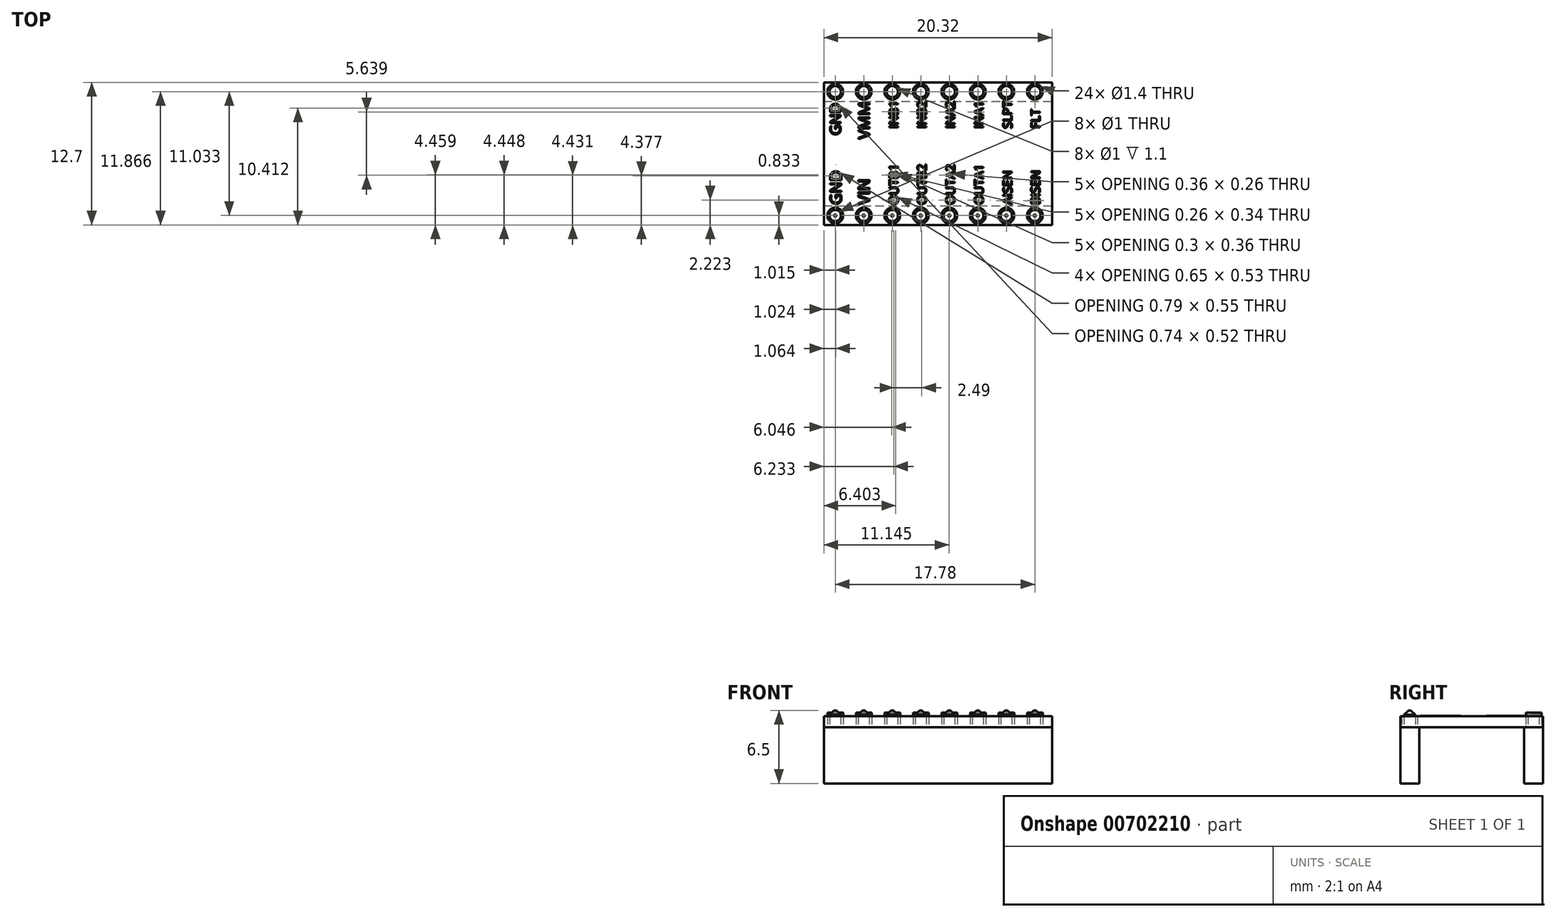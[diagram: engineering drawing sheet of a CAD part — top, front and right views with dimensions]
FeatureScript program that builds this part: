
annotation { "Feature Type Name" : "Feature", "Feature Type Description" : "" }
export const myFeature = defineFeature(function(context is Context, id is Id, definition is map)
    precondition{}
    {
        {
            var Q0;
            Q0=qCreatedBy(makeId("Top.planeOp"),FACE);
            cPlane(context, id + "F0", {"entities" : qUnion([Q0]), "cplaneType" : CPlaneType.OFFSET, "offset" : 5 * mm, "width" : 150 * mm, "height" : 150 * mm});
        }
        {
            var Q0;
            Q0=qCreatedBy(id+"F0.planeOp",FACE);
            var sketch = newSketch(context, id + "F1", { "sketchPlane" : qUnion([Q0])});
            skLineSegment(sketch, "E0.bottom", {"start": v(-10.16, 6.35) * mm, "end": v(10.16, 6.35) * mm});
            skLineSegment(sketch, "E0.top", {"start": v(-10.16, -6.35) * mm, "end": v(10.16, -6.35) * mm});
            skLineSegment(sketch, "E0.left", {"start": v(-10.16, 6.35) * mm, "end": v(-10.16, -6.35) * mm});
            skLineSegment(sketch, "E0.right", {"start": v(10.16, 6.35) * mm, "end": v(10.16, -6.35) * mm});
            skPoint(sketch, "E0.middle", {"position": v(0, 0) * mm});
            skCircle(sketch, "E1", {"center": v(-9.15, -5.52) * mm, "radius": 0.5 * mm});
            skCircle(sketch, "E2.0", {"center": v(-9.15, -5.52) * mm, "radius": 0.7 * mm});
            skCircle(sketch, "E3.1.0.0", {"center": v(-6.6, -5.52) * mm, "radius": 0.5 * mm});
            skCircle(sketch, "E3.1.0.1", {"center": v(-6.6, -5.52) * mm, "radius": 0.7 * mm});
            skCircle(sketch, "E3.2.0.0", {"center": v(-4.07, -5.52) * mm, "radius": 0.5 * mm});
            skCircle(sketch, "E3.2.0.1", {"center": v(-4.07, -5.52) * mm, "radius": 0.7 * mm});
            skCircle(sketch, "E3.3.0.0", {"center": v(-1.53, -5.52) * mm, "radius": 0.5 * mm});
            skCircle(sketch, "E3.3.0.1", {"center": v(-1.53, -5.52) * mm, "radius": 0.7 * mm});
            skCircle(sketch, "E3.4.0.0", {"center": v(1.01, -5.52) * mm, "radius": 0.5 * mm});
            skCircle(sketch, "E3.4.0.1", {"center": v(1.01, -5.52) * mm, "radius": 0.7 * mm});
            skCircle(sketch, "E3.5.0.0", {"center": v(3.55, -5.52) * mm, "radius": 0.5 * mm});
            skCircle(sketch, "E3.5.0.1", {"center": v(3.55, -5.52) * mm, "radius": 0.7 * mm});
            skCircle(sketch, "E3.6.0.0", {"center": v(6.1, -5.52) * mm, "radius": 0.5 * mm});
            skCircle(sketch, "E3.6.0.1", {"center": v(6.1, -5.52) * mm, "radius": 0.7 * mm});
            skCircle(sketch, "E3.7.0.0", {"center": v(8.63, -5.52) * mm, "radius": 0.5 * mm});
            skCircle(sketch, "E3.7.0.1", {"center": v(8.63, -5.52) * mm, "radius": 0.7 * mm});
            skLineSegment(sketch, "E3.direction1", {"start": v(-9.15, -5.52) * mm, "end": v(-6.6, -5.52) * mm, "construction": true});
            skCircle(sketch, "E4.MirrorC", {"center": v(-9.15, 5.52) * mm, "radius": 0.5 * mm});
            skCircle(sketch, "E5.MirrorC", {"center": v(-9.15, 5.52) * mm, "radius": 0.7 * mm});
            skCircle(sketch, "E6.MirrorC", {"center": v(-6.6, 5.52) * mm, "radius": 0.7 * mm});
            skCircle(sketch, "E7.MirrorC", {"center": v(-6.6, 5.52) * mm, "radius": 0.5 * mm});
            skCircle(sketch, "E8.MirrorC", {"center": v(-4.07, 5.52) * mm, "radius": 0.7 * mm});
            skCircle(sketch, "E9.MirrorC", {"center": v(-4.07, 5.52) * mm, "radius": 0.5 * mm});
            skCircle(sketch, "E10.MirrorC", {"center": v(-1.53, 5.52) * mm, "radius": 0.7 * mm});
            skCircle(sketch, "E11.MirrorC", {"center": v(-1.53, 5.52) * mm, "radius": 0.5 * mm});
            skCircle(sketch, "E12.MirrorC", {"center": v(1.01, 5.52) * mm, "radius": 0.7 * mm});
            skCircle(sketch, "E13.MirrorC", {"center": v(1.01, 5.52) * mm, "radius": 0.5 * mm});
            skCircle(sketch, "E14.MirrorC", {"center": v(3.55, 5.52) * mm, "radius": 0.5 * mm});
            skCircle(sketch, "E15.MirrorC", {"center": v(3.55, 5.52) * mm, "radius": 0.7 * mm});
            skCircle(sketch, "E16.MirrorC", {"center": v(6.1, 5.52) * mm, "radius": 0.7 * mm});
            skCircle(sketch, "E17.MirrorC", {"center": v(6.1, 5.52) * mm, "radius": 0.5 * mm});
            skCircle(sketch, "E18.MirrorC", {"center": v(8.63, 5.52) * mm, "radius": 0.7 * mm});
            skCircle(sketch, "E19.MirrorC", {"center": v(8.63, 5.52) * mm, "radius": 0.5 * mm});
            skSolve(sketch);
        }
        {
            var Q0;
            Q0=makeQuery(id+"F1.imprint","IMPRINT",FACE,{"disambiguationData":[TD([[makeQuery(id+"F1.imprint","IMPRINT",EDGE,{"derivedFrom":sQuery(id+"F1.wireOp",EDGE,"E0.bottom")}),-1.0]])]});
            extrude(context, id + "F2", {"entities" : qUnion([Q0]), "depth" : 1 * mm, "offsetDistance" : 25 * mm});
        }
        {
            var Q0;
            Q0=makeQuery(id+"F1.imprint","IMPRINT",FACE,{"disambiguationData":[TD([[makeQuery(id+"F1.imprint","IMPRINT",EDGE,{"derivedFrom":sQuery(id+"F1.wireOp",EDGE,"E4.MirrorC")}),1.0]])]});
            var Q1;
            Q1=makeQuery(id+"F1.imprint","IMPRINT",FACE,{"disambiguationData":[TD([[makeQuery(id+"F1.imprint","IMPRINT",EDGE,{"derivedFrom":sQuery(id+"F1.wireOp",EDGE,"E6.MirrorC")}),-1.0]])]});
            var Q2;
            Q2=makeQuery(id+"F1.imprint","IMPRINT",FACE,{"disambiguationData":[TD([[makeQuery(id+"F1.imprint","IMPRINT",EDGE,{"derivedFrom":sQuery(id+"F1.wireOp",EDGE,"E8.MirrorC")}),-1.0]])]});
            var Q3;
            Q3=makeQuery(id+"F1.imprint","IMPRINT",FACE,{"disambiguationData":[TD([[makeQuery(id+"F1.imprint","IMPRINT",EDGE,{"derivedFrom":sQuery(id+"F1.wireOp",EDGE,"E10.MirrorC")}),-1.0]])]});
            var Q4;
            Q4=makeQuery(id+"F1.imprint","IMPRINT",FACE,{"disambiguationData":[TD([[makeQuery(id+"F1.imprint","IMPRINT",EDGE,{"derivedFrom":sQuery(id+"F1.wireOp",EDGE,"E12.MirrorC")}),-1.0]])]});
            var Q5;
            Q5=makeQuery(id+"F1.imprint","IMPRINT",FACE,{"disambiguationData":[TD([[makeQuery(id+"F1.imprint","IMPRINT",EDGE,{"derivedFrom":sQuery(id+"F1.wireOp",EDGE,"E14.MirrorC")}),1.0]])]});
            var Q6;
            Q6=makeQuery(id+"F1.imprint","IMPRINT",FACE,{"disambiguationData":[TD([[makeQuery(id+"F1.imprint","IMPRINT",EDGE,{"derivedFrom":sQuery(id+"F1.wireOp",EDGE,"E16.MirrorC")}),-1.0]])]});
            var Q7;
            Q7=makeQuery(id+"F1.imprint","IMPRINT",FACE,{"disambiguationData":[TD([[makeQuery(id+"F1.imprint","IMPRINT",EDGE,{"derivedFrom":sQuery(id+"F1.wireOp",EDGE,"E18.MirrorC")}),-1.0]])]});
            var Q8;
            Q8=makeQuery(id+"F1.imprint","IMPRINT",FACE,{"disambiguationData":[TD([[makeQuery(id+"F1.imprint","IMPRINT",EDGE,{"derivedFrom":sQuery(id+"F1.wireOp",EDGE,"E3.7.0.0")}),-1.0]])]});
            var Q9;
            Q9=makeQuery(id+"F1.imprint","IMPRINT",FACE,{"disambiguationData":[TD([[makeQuery(id+"F1.imprint","IMPRINT",EDGE,{"derivedFrom":sQuery(id+"F1.wireOp",EDGE,"E3.6.0.0")}),-1.0]])]});
            var Q10;
            Q10=makeQuery(id+"F1.imprint","IMPRINT",FACE,{"disambiguationData":[TD([[makeQuery(id+"F1.imprint","IMPRINT",EDGE,{"derivedFrom":sQuery(id+"F1.wireOp",EDGE,"E3.5.0.0")}),-1.0]])]});
            var Q11;
            Q11=makeQuery(id+"F1.imprint","IMPRINT",FACE,{"disambiguationData":[TD([[makeQuery(id+"F1.imprint","IMPRINT",EDGE,{"derivedFrom":sQuery(id+"F1.wireOp",EDGE,"E3.4.0.0")}),-1.0]])]});
            var Q12;
            Q12=makeQuery(id+"F1.imprint","IMPRINT",FACE,{"disambiguationData":[TD([[makeQuery(id+"F1.imprint","IMPRINT",EDGE,{"derivedFrom":sQuery(id+"F1.wireOp",EDGE,"E3.3.0.0")}),-1.0]])]});
            var Q13;
            Q13=makeQuery(id+"F1.imprint","IMPRINT",FACE,{"disambiguationData":[TD([[makeQuery(id+"F1.imprint","IMPRINT",EDGE,{"derivedFrom":sQuery(id+"F1.wireOp",EDGE,"E3.2.0.0")}),-1.0]])]});
            var Q14;
            Q14=makeQuery(id+"F1.imprint","IMPRINT",FACE,{"disambiguationData":[TD([[makeQuery(id+"F1.imprint","IMPRINT",EDGE,{"derivedFrom":sQuery(id+"F1.wireOp",EDGE,"E3.1.0.0")}),-1.0]])]});
            var Q15;
            Q15=makeQuery(id+"F1.imprint","IMPRINT",FACE,{"disambiguationData":[TD([[makeQuery(id+"F1.imprint","IMPRINT",EDGE,{"derivedFrom":sQuery(id+"F1.wireOp",EDGE,"E1")}),-1.0]])]});
            extrude(context, id + "F3", {"entities" : qUnion([Q0, Q1, Q2, Q3, Q4, Q5, Q6, Q7, Q8, Q9, Q10, Q11, Q12, Q13, Q14, Q15]), "depth" : 1 * mm, "offsetDistance" : 25 * mm});
        }
        {
            var Q0;
            Q0=qCreatedBy(id+"F0.planeOp",FACE);
            cPlane(context, id + "F4", {"entities" : qUnion([Q0]), "cplaneType" : CPlaneType.OFFSET, "offset" : 1 * mm, "width" : 150 * mm, "height" : 150 * mm});
        }
        {
            var Q0;
            Q0=qCreatedBy(id+"F4.planeOp",FACE);
            var sketch = newSketch(context, id + "F5", { "sketchPlane" : qUnion([Q0])});
            skText(sketch, "E20", { "text": "GND", "fontName": "OpenSans-Regular.ttf"});
            skText(sketch, "E21", { "text": "GND", "fontName": "OpenSans-Regular.ttf"});
            skText(sketch, "E22", { "text": "VIN", "fontName": "OpenSans-Regular.ttf"});
            skText(sketch, "E23", { "text": "VMM", "fontName": "OpenSans-Regular.ttf"});
            skText(sketch, "E24", { "text": "OUTB1", "fontName": "OpenSans-Regular.ttf"});
            skText(sketch, "E25", { "text": "OUTB2", "fontName": "OpenSans-Regular.ttf"});
            skText(sketch, "E26", { "text": "OUTA1", "fontName": "OpenSans-Regular.ttf"});
            skText(sketch, "E27", { "text": "OUTA2", "fontName": "OpenSans-Regular.ttf"});
            skText(sketch, "E28", { "text": "AISEN", "fontName": "OpenSans-Regular.ttf"});
            skText(sketch, "E29", { "text": "BISEN", "fontName": "OpenSans-Regular.ttf"});
            skText(sketch, "E30", { "text": "INA1", "fontName": "OpenSans-Regular.ttf"});
            skText(sketch, "E31", { "text": "INA2", "fontName": "OpenSans-Regular.ttf"});
            skText(sketch, "E32", { "text": "INB1", "fontName": "OpenSans-Regular.ttf"});
            skText(sketch, "E33", { "text": "INB2", "fontName": "OpenSans-Regular.ttf"});
            skText(sketch, "E34", { "text": "SLPT", "fontName": "OpenSans-Regular.ttf"});
            skText(sketch, "E35", { "text": "FLT", "fontName": "OpenSans-Regular.ttf"});
            const initialGuessF5  = {"E20": [-0.0086, -0.00456, 0, 1, 0.001], "E21": [-0.00867, 0.00163, 0, 1, 0.00094], "E22": [-0.00608, -0.00456, 0, 1, 0.00103], "E23": [-0.00608, 0.00129, 0, 1, 0.001], "E24": [-0.00353, -0.00456, 0, 1, 0.0008], "E25": [-0.00104, -0.00456, 0, 1, 0.0008], "E26": [0.00405, -0.00456, 0, 1, 0.0008], "E27": [0.0015, -0.00456, 0, 1, 0.0008], "E28": [0.0066, -0.00456, 0, 1, 0.0008], "E29": [0.00908, -0.00456, 0, 1, 0.0008], "E30": [0.00405, 0.00222, 0, 1, 0.0008], "E31": [0.0015, 0.00222, 0, 1, 0.0008], "E32": [-0.00353, 0.00222, 0, 1, 0.0008], "E33": [-0.00104, 0.00222, 0, 1, 0.0008], "E34": [0.0066, 0.00222, 0, 1, 0.0008], "E35": [0.00908, 0.00222, 0, 1, 0.0008]};
            skSetInitialGuess(sketch, initialGuessF5);
            skSolve(sketch);
        }
        {
            var Q0;
            Q0 = qSketchRegion(id + "F5", true);
            extrude(context, id + "F6", {"entities" : qUnion([Q0]), "depth" : 0.01 * mm, "offsetDistance" : 25 * mm});
        }
        {
            var Q0;
            Q0=makeQuery(id+"F1.imprint","IMPRINT",FACE,{"disambiguationData":[TD([[makeQuery(id+"F1.imprint","IMPRINT",EDGE,{"derivedFrom":sQuery(id+"F1.wireOp",EDGE,"E4.MirrorC")}),-1.0]])]});
            var Q1;
            Q1=makeQuery(id+"F1.imprint","IMPRINT",FACE,{"disambiguationData":[TD([[makeQuery(id+"F1.imprint","IMPRINT",EDGE,{"derivedFrom":sQuery(id+"F1.wireOp",EDGE,"E7.MirrorC")}),-1.0]])]});
            var Q2;
            Q2=makeQuery(id+"F1.imprint","IMPRINT",FACE,{"disambiguationData":[TD([[makeQuery(id+"F1.imprint","IMPRINT",EDGE,{"derivedFrom":sQuery(id+"F1.wireOp",EDGE,"E9.MirrorC")}),-1.0]])]});
            var Q3;
            Q3=makeQuery(id+"F1.imprint","IMPRINT",FACE,{"disambiguationData":[TD([[makeQuery(id+"F1.imprint","IMPRINT",EDGE,{"derivedFrom":sQuery(id+"F1.wireOp",EDGE,"E11.MirrorC")}),-1.0]])]});
            var Q4;
            Q4=makeQuery(id+"F1.imprint","IMPRINT",FACE,{"disambiguationData":[TD([[makeQuery(id+"F1.imprint","IMPRINT",EDGE,{"derivedFrom":sQuery(id+"F1.wireOp",EDGE,"E13.MirrorC")}),-1.0]])]});
            var Q5;
            Q5=makeQuery(id+"F1.imprint","IMPRINT",FACE,{"disambiguationData":[TD([[makeQuery(id+"F1.imprint","IMPRINT",EDGE,{"derivedFrom":sQuery(id+"F1.wireOp",EDGE,"E14.MirrorC")}),-1.0]])]});
            var Q6;
            Q6=makeQuery(id+"F1.imprint","IMPRINT",FACE,{"disambiguationData":[TD([[makeQuery(id+"F1.imprint","IMPRINT",EDGE,{"derivedFrom":sQuery(id+"F1.wireOp",EDGE,"E17.MirrorC")}),-1.0]])]});
            var Q7;
            Q7=makeQuery(id+"F1.imprint","IMPRINT",FACE,{"disambiguationData":[TD([[makeQuery(id+"F1.imprint","IMPRINT",EDGE,{"derivedFrom":sQuery(id+"F1.wireOp",EDGE,"E19.MirrorC")}),-1.0]])]});
            var Q8;
            Q8=makeQuery(id+"F1.imprint","IMPRINT",FACE,{"disambiguationData":[TD([[makeQuery(id+"F1.imprint","IMPRINT",EDGE,{"derivedFrom":sQuery(id+"F1.wireOp",EDGE,"E3.7.0.0")}),1.0]])]});
            var Q9;
            Q9=makeQuery(id+"F1.imprint","IMPRINT",FACE,{"disambiguationData":[TD([[makeQuery(id+"F1.imprint","IMPRINT",EDGE,{"derivedFrom":sQuery(id+"F1.wireOp",EDGE,"E3.6.0.0")}),1.0]])]});
            var Q10;
            Q10=makeQuery(id+"F1.imprint","IMPRINT",FACE,{"disambiguationData":[TD([[makeQuery(id+"F1.imprint","IMPRINT",EDGE,{"derivedFrom":sQuery(id+"F1.wireOp",EDGE,"E3.5.0.0")}),1.0]])]});
            var Q11;
            Q11=makeQuery(id+"F1.imprint","IMPRINT",FACE,{"disambiguationData":[TD([[makeQuery(id+"F1.imprint","IMPRINT",EDGE,{"derivedFrom":sQuery(id+"F1.wireOp",EDGE,"E3.4.0.0")}),1.0]])]});
            var Q12;
            Q12=makeQuery(id+"F1.imprint","IMPRINT",FACE,{"disambiguationData":[TD([[makeQuery(id+"F1.imprint","IMPRINT",EDGE,{"derivedFrom":sQuery(id+"F1.wireOp",EDGE,"E3.3.0.0")}),1.0]])]});
            var Q13;
            Q13=makeQuery(id+"F1.imprint","IMPRINT",FACE,{"disambiguationData":[TD([[makeQuery(id+"F1.imprint","IMPRINT",EDGE,{"derivedFrom":sQuery(id+"F1.wireOp",EDGE,"E3.2.0.0")}),1.0]])]});
            var Q14;
            Q14=makeQuery(id+"F1.imprint","IMPRINT",FACE,{"disambiguationData":[TD([[makeQuery(id+"F1.imprint","IMPRINT",EDGE,{"derivedFrom":sQuery(id+"F1.wireOp",EDGE,"E3.1.0.0")}),1.0]])]});
            var Q15;
            Q15=makeQuery(id+"F1.imprint","IMPRINT",FACE,{"disambiguationData":[TD([[makeQuery(id+"F1.imprint","IMPRINT",EDGE,{"derivedFrom":sQuery(id+"F1.wireOp",EDGE,"E1")}),1.0]])]});
            extrude(context, id + "F7", {"entities" : qUnion([Q0, Q1, Q2, Q3, Q4, Q5, Q6, Q7, Q8, Q9, Q10, Q11, Q12, Q13, Q14, Q15]), "depth" : 1.5 * mm, "offsetDistance" : 25 * mm});
        }
        {
            var Q0;
            Q0=makeQuery(id+"F7.opExtrude","CAP_EDGE",EDGE,{"disambiguationData":[OSD([sQuery(id+"F1.wireOp",EDGE,"E1")])],"isStart":false});
            var Q1;
            Q1=makeQuery(id+"F7.opExtrude","CAP_EDGE",EDGE,{"disambiguationData":[OSD([sQuery(id+"F1.wireOp",EDGE,"E3.1.0.0")])],"isStart":false});
            var Q2;
            Q2=makeQuery(id+"F7.opExtrude","CAP_EDGE",EDGE,{"disambiguationData":[OSD([sQuery(id+"F1.wireOp",EDGE,"E3.2.0.0")])],"isStart":false});
            var Q3;
            Q3=makeQuery(id+"F7.opExtrude","CAP_EDGE",EDGE,{"disambiguationData":[OSD([sQuery(id+"F1.wireOp",EDGE,"E3.3.0.0")])],"isStart":false});
            var Q4;
            Q4=makeQuery(id+"F7.opExtrude","CAP_EDGE",EDGE,{"disambiguationData":[OSD([sQuery(id+"F1.wireOp",EDGE,"E3.4.0.0")])],"isStart":false});
            var Q5;
            Q5=makeQuery(id+"F7.opExtrude","CAP_EDGE",EDGE,{"disambiguationData":[OSD([sQuery(id+"F1.wireOp",EDGE,"E3.5.0.0")])],"isStart":false});
            var Q6;
            Q6=makeQuery(id+"F7.opExtrude","CAP_EDGE",EDGE,{"disambiguationData":[OSD([sQuery(id+"F1.wireOp",EDGE,"E3.6.0.0")])],"isStart":false});
            var Q7;
            Q7=makeQuery(id+"F7.opExtrude","CAP_EDGE",EDGE,{"disambiguationData":[OSD([sQuery(id+"F1.wireOp",EDGE,"E3.7.0.0")])],"isStart":false});
            var Q8;
            Q8=makeQuery(id+"F7.opExtrude","CAP_EDGE",EDGE,{"disambiguationData":[OSD([sQuery(id+"F1.wireOp",EDGE,"E4.MirrorC")])],"isStart":false});
            var Q9;
            Q9=makeQuery(id+"F7.opExtrude","CAP_EDGE",EDGE,{"disambiguationData":[OSD([sQuery(id+"F1.wireOp",EDGE,"E7.MirrorC")])],"isStart":false});
            var Q10;
            Q10=makeQuery(id+"F7.opExtrude","CAP_EDGE",EDGE,{"disambiguationData":[OSD([sQuery(id+"F1.wireOp",EDGE,"E9.MirrorC")])],"isStart":false});
            var Q11;
            Q11=makeQuery(id+"F7.opExtrude","CAP_EDGE",EDGE,{"disambiguationData":[OSD([sQuery(id+"F1.wireOp",EDGE,"E11.MirrorC")])],"isStart":false});
            var Q12;
            Q12=makeQuery(id+"F7.opExtrude","CAP_EDGE",EDGE,{"disambiguationData":[OSD([sQuery(id+"F1.wireOp",EDGE,"E13.MirrorC")])],"isStart":false});
            var Q13;
            Q13=makeQuery(id+"F7.opExtrude","CAP_EDGE",EDGE,{"disambiguationData":[OSD([sQuery(id+"F1.wireOp",EDGE,"E14.MirrorC")])],"isStart":false});
            var Q14;
            Q14=makeQuery(id+"F7.opExtrude","CAP_EDGE",EDGE,{"disambiguationData":[OSD([sQuery(id+"F1.wireOp",EDGE,"E17.MirrorC")])],"isStart":false});
            var Q15;
            Q15=makeQuery(id+"F7.opExtrude","CAP_EDGE",EDGE,{"disambiguationData":[OSD([sQuery(id+"F1.wireOp",EDGE,"E19.MirrorC")])],"isStart":false});
            chamfer(context, id + "F8", {"entities" : qUnion([Q0, Q1, Q2, Q3, Q4, Q5, Q6, Q7, Q8, Q9, Q10, Q11, Q12, Q13, Q14, Q15]), "width" : 0.4 * mm, "tangentPropagation" : true});
        }
        {
            var Q0;
            Q0=qCreatedBy(makeId("Top.planeOp"),FACE);
            var sketch = newSketch(context, id + "F9", { "sketchPlane" : qUnion([Q0])});
            skLineSegment(sketch, "E36.bottom", {"start": v(-10.16, 6.35) * mm, "end": v(10.16, 6.35) * mm});
            skLineSegment(sketch, "E36.top", {"start": v(-10.16, -6.35) * mm, "end": v(10.16, -6.35) * mm});
            skLineSegment(sketch, "E36.left", {"start": v(-10.16, 6.35) * mm, "end": v(-10.16, 4.66) * mm});
            skLineSegment(sketch, "E36.right", {"start": v(10.16, 6.35) * mm, "end": v(10.16, 4.66) * mm});
            skPoint(sketch, "E36.middle", {"position": v(0, 0) * mm});
            skLineSegment(sketch, "E37", {"start": v(-10.16, 4.66) * mm, "end": v(10.16, 4.66) * mm});
            skLineSegment(sketch, "E38.MirrorCS", {"start": v(-10.16, -4.66) * mm, "end": v(10.16, -4.66) * mm});
            skLineSegment(sketch, "E39.trimOffspring", {"start": v(-10.16, -4.66) * mm, "end": v(-10.16, -6.35) * mm});
            skLineSegment(sketch, "E40.trimOffspring", {"start": v(10.16, -4.66) * mm, "end": v(10.16, -6.35) * mm});
            skSolve(sketch);
        }
        {
            var Q0;
            Q0=makeQuery(id+"F9.imprint","IMPRINT",FACE,{"disambiguationData":[TD([[makeQuery(id+"F9.imprint","IMPRINT",EDGE,{"derivedFrom":sQuery(id+"F9.wireOp",EDGE,"E36.bottom")}),-1.0]])]});
            var Q1;
            Q1=makeQuery(id+"F9.imprint","IMPRINT",FACE,{"disambiguationData":[TD([[makeQuery(id+"F9.imprint","IMPRINT",EDGE,{"derivedFrom":sQuery(id+"F9.wireOp",EDGE,"E36.top")}),1.0]])]});
            extrude(context, id + "F10", {"entities" : qUnion([Q0, Q1]), "depth" : 5 * mm, "offsetDistance" : 25 * mm});
        }
    });
